# Revit family: Flushometer-Urinal_Touchless-KOHLER-MACH_WAVE-K-40UD00K20_1
name_source: partatom
category: Plumbing Fixtures
revit_build: Autodesk Revit 2017 (Build: 20160225_1515(x64)
units: mm (PartAtom-declared; Revit-internal decimal feet)

## family parameters
Cut with Voids When Loaded = No
Host = Face
OmniClass Number = 23.27.31.00
OmniClass Title = Valves
Part Type = Normal
Room Calculation Point = No
Round Connector Dimension = Use Diameter
Shared = No

## types (1)
- CP-Polished Chrome
    ADA Compliant = No
    Assembly Code = D2020
    CW Connection = Yes
    Cold Water Inlet = Cold Water Inlet
    Cold Water Outlet = Cold Water Outlet
    Date Modified = 02/09/2021
    Default Elevation = 0"
    Description = DC 1.0 GPF URINAL FLUSH VALVE
    Finish = Kohler-Metal-CP-Polished_Chrome
    Flow Rate = 0 GPM
    Flush Rate- GPF = 1.0 GPF
    Flush Rate- LPF = 3.8 LPF
    HW Connection = No
    Hot Water Inlet = Hot Water Inlet
    Manufacturer = KOHLER Co.
    Master Format 2014 = 23 09 13.33
    Master Format 2014 Name = Control Valves
    Material = Premium Metal Construction
    Model = K-40UD00K20-CP
    Pressure = 0.00 psi
    Product Documentation Link = https://www.us.kohler.com
    Product Name = MACH WAVE
    Product Page URL = http://www.us.kohler.com
    Type = 1
    URL = https://www.us.kohler.com
    Vent Connection = No
    Waste Connection = No
    Waste Water Outlet = Waste Water Outlet
    WaterSense Certified = No

## geometry (parser evidence)
native form markers: Sweep x3
no freeform markers — native parametric forms only
